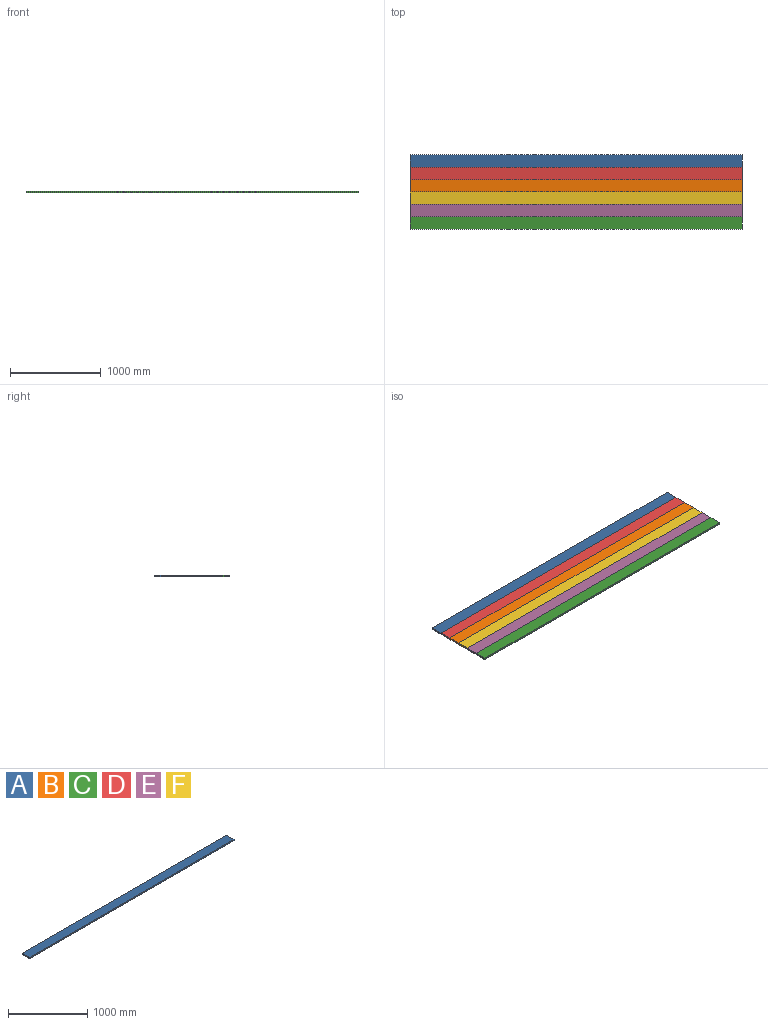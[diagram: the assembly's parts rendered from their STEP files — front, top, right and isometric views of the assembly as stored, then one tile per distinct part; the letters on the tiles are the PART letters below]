
ASSEMBLY  parts=6 mates=15
PART A: 6 faces, bbox 3657.6x136.5x19.1 mm
  f0: plane 136.53x19.05mm, normal (-1,0,0), area 2600.8mm2, adj f1,f3,f4,f5
  f1: plane 3657.6x19.05mm, normal (0,-1,0), area 69677.3mm2, adj f0,f2,f4,f5
  f2: plane 136.53x19.05mm, normal (1,0,0), area 2600.8mm2, adj f1,f3,f4,f5
  f3: plane 3657.6x19.05mm, normal (0,1,0), area 69677.3mm2, adj f0,f2,f4,f5
  f4: plane 3657.6x136.53mm, normal (0,0,1), area 499353.8mm2, adj f0,f1,f2,f3
  f5: plane 3657.6x136.53mm, normal (0,0,-1), area 499353.8mm2, adj f0,f1,f2,f3
PART B: same geometry as A
PART C: same geometry as A
PART D: same geometry as A
PART E: same geometry as A
PART F: same geometry as A
PLACE A t=(-1921.68,1310.89,-180.33)mm
PLACE B t=(-1921.68,1037.84,-180.33)mm
PLACE C t=(-1921.68,628.26,-180.33)mm
PLACE D t=(-1921.68,1174.36,-180.33)mm
PLACE E t=(-1921.68,764.79,-180.33)mm
PLACE F t=(-1921.68,901.31,-180.33)mm
MATE planar F.f1 <-> E.f3  axis (0,-1,0) through (-92.88,901.31,-170.8)mm
MATE planar D.f4 <-> A.f4  axis (0,0,1) through (-92.88,1242.63,-161.28)mm
MATE planar F.f3 <-> B.f1  axis (0,1,0) through (-92.88,1037.84,-170.8)mm
MATE planar C.f4 <-> E.f4  axis (0,0,1) through (-92.88,696.53,-161.28)mm
MATE planar B.f0 <-> F.f0  axis (-1,0,0) through (-1921.68,1106.1,-170.8)mm
MATE planar D.f3 <-> A.f1  axis (0,1,0) through (-92.88,1310.89,-170.8)mm
MATE planar D.f1 <-> B.f3  axis (0,-1,0) through (-92.88,1174.36,-170.8)mm
MATE planar C.f0 <-> F.f0  axis (-1,0,0) through (-1921.68,696.53,-170.8)mm
MATE planar D.f2 <-> A.f2  axis (1,0,0) through (1735.92,1242.63,-170.8)mm
MATE planar D.f2 <-> B.f2  axis (1,0,0) through (1735.92,1242.63,-170.8)mm
MATE planar E.f4 <-> F.f4  axis (0,0,1) through (-92.88,833.05,-161.28)mm
MATE planar B.f0 <-> E.f0  axis (-1,0,0) through (-1921.68,1106.1,-170.8)mm
MATE planar E.f1 <-> C.f3  axis (0,-1,0) through (-92.88,764.79,-170.8)mm
MATE planar E.f4 <-> B.f4  axis (0,0,1) through (-92.88,833.05,-161.28)mm
MATE planar D.f4 <-> B.f4  axis (0,0,1) through (1735.92,1174.36,-161.28)mm
